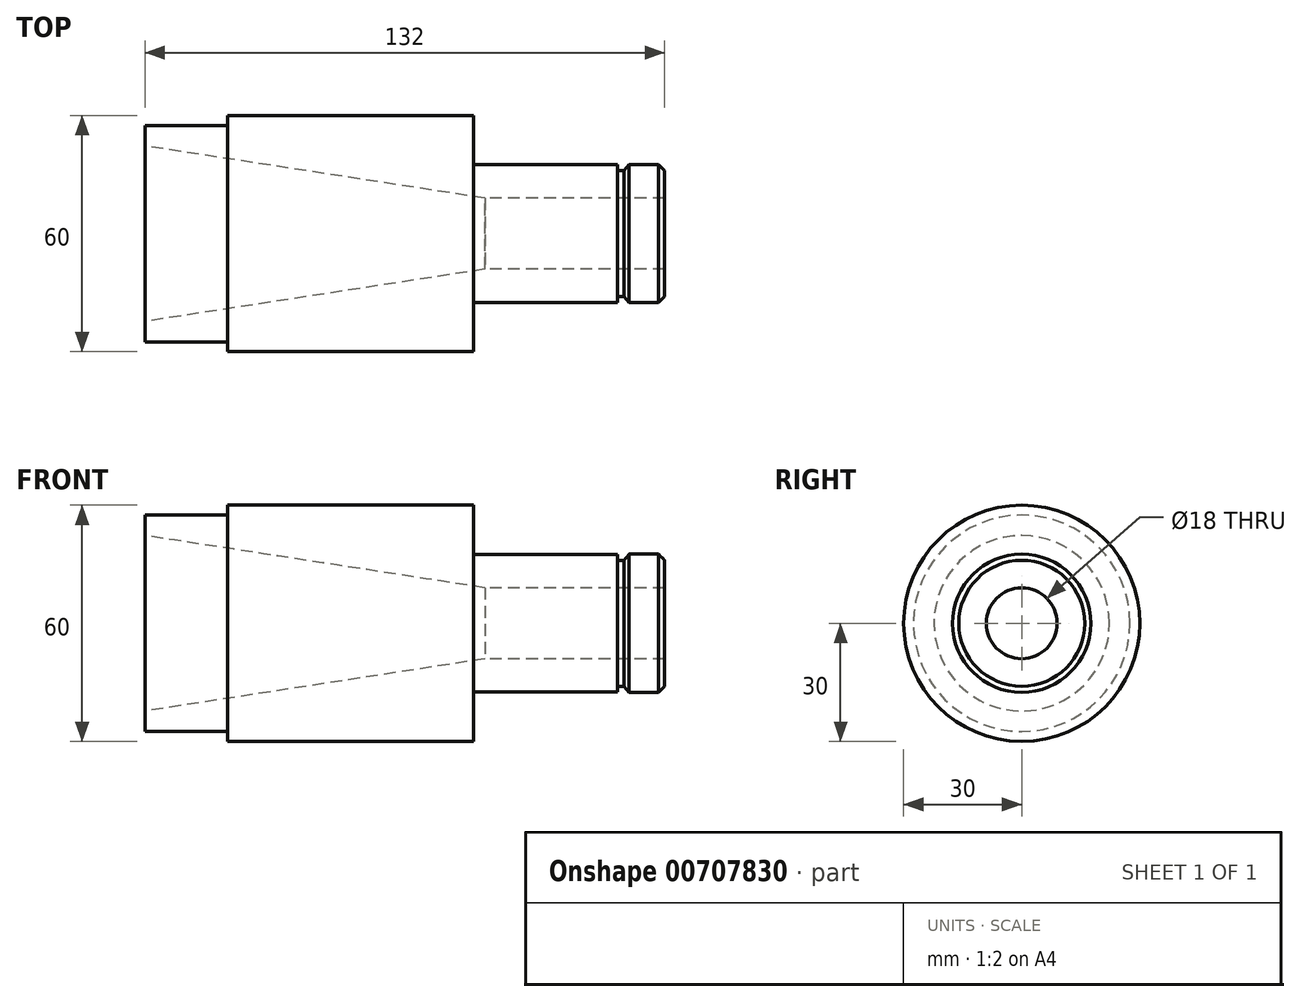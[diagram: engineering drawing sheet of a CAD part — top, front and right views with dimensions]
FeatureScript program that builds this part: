
annotation { "Feature Type Name" : "Feature", "Feature Type Description" : "" }
export const myFeature = defineFeature(function(context is Context, id is Id, definition is map)
    precondition{}
    {
        {
            var Q0;
            Q0=qCreatedBy(makeId("Front.planeOp"),FACE);
            var sketch = newSketch(context, id + "F0", { "sketchPlane" : qUnion([Q0])});
            skLineSegment(sketch, "E0", {"start": v(-141, 0) * mm, "end": v(59, 0) * mm, "construction": true});
            skLineSegment(sketch, "E1", {"start": v(-120, 27.5) * mm, "end": v(-120, 22.3) * mm});
            skLineSegment(sketch, "E2", {"start": v(-120, 22.3) * mm, "end": v(-33.59, 9) * mm});
            skLineSegment(sketch, "E3", {"start": v(0, 17.5) * mm, "end": v(0, 16) * mm});
            skLineSegment(sketch, "E4", {"start": v(0, 9) * mm, "end": v(-33.59, 9) * mm});
            skLineSegment(sketch, "E5", {"start": v(-120, 27.5) * mm, "end": v(-99, 27.5) * mm});
            skLineSegment(sketch, "E6", {"start": v(-36.5, 17.5) * mm, "end": v(0, 17.5) * mm});
            skLineSegment(sketch, "E7", {"start": v(-36.5, 30) * mm, "end": v(-36.5, 17.5) * mm});
            skLineSegment(sketch, "E8", {"start": v(0, 9) * mm, "end": v(12, 9) * mm});
            skLineSegment(sketch, "E9", {"start": v(12, 9) * mm, "end": v(12, 16) * mm});
            skLineSegment(sketch, "E10", {"start": v(1.66, 16) * mm, "end": v(0, 16) * mm});
            skLineSegment(sketch, "E11", {"start": v(-99, 27.5) * mm, "end": v(-99, 30) * mm});
            skLineSegment(sketch, "E12", {"start": v(-99, 30) * mm, "end": v(-36.5, 30) * mm});
            skLineSegment(sketch, "E13", {"start": v(1.66, 16) * mm, "end": v(2.99, 17.57) * mm});
            skLineSegment(sketch, "E14", {"start": v(2.99, 17.57) * mm, "end": v(10.45, 17.57) * mm});
            skLineSegment(sketch, "E15", {"start": v(12, 16) * mm, "end": v(10.45, 17.57) * mm});
            skSolve(sketch);
        }
        {
            var Q0;
            Q0 = qSketchRegion(id + "F0", true);
            var Q1;
            Q1=sQuery(id+"F0.wireOp",EDGE,"E0");
            revolve(context, id + "F1", {"surfaceOperationType" : NewSurfaceOperationType.NEW, "entities" : qUnion([Q0]), "axis" : qUnion([Q1]), "revolveType" : RevolveType.FULL});
        }
    });
